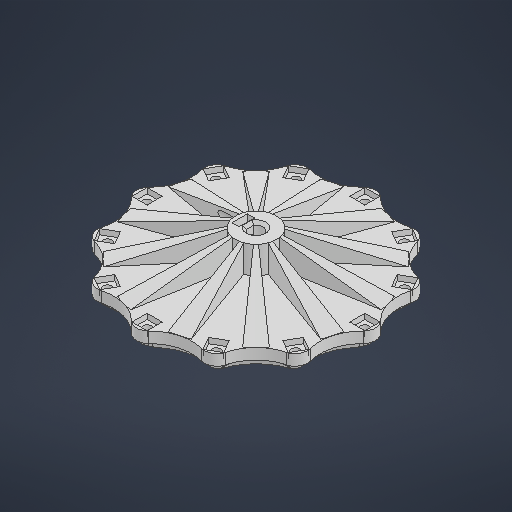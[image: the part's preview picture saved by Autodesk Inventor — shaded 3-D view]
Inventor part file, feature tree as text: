
AUTODESK INVENTOR PART (.ipt)
format: ipt  version: 2025.1 (Build 291241000, 241)  size: 1,274,880 bytes
history: native  units: mm
features: extrude x10, sketch x8, projected_geometry x4, plane x3, pattern_circular x2, chamfer x2, revolve x1
ambient origin geometry x8: Origin, YZ Plane, XZ Plane, XY Plane, X Axis, Y Axis, Z Axis, Center Point
bodies: Solid1 (feature_tree)
feature tree (30):
  sketch  "Sketch1"  dims[d0=5.2mm d3=15.0mm]
  extrude  "Extrusion1"  Depth=15.0mm
  extrude  "Extrusion2"  Depth=3.0mm TaperAngle=0.0deg
  extrude  "Extrusion3"  Depth=10.0mm
  sketch  "Sketch3"  dims[d7=10.0mm d8=0.0mm d9=3.2mm]
  plane  "Work Plane2"
  extrude  "Extrusion4"  TaperAngle=0.0deg  [1 undecoded]
  extrude  "Extrusion5"  Depth=5.65mm
  extrude  "Extrusion7"  Depth=10.0mm
  extrude  "Extrusion11"  TaperAngle=0.0deg  [1 undecoded]
  pattern_circular  "Circular Pattern1"  Count=12 Angle=360.0deg
  sketch  "Sketch4"  dims[d10=5.0mm d11=0.0mm d12=0.0mm]
  plane  "Work Plane3"
  revolve  "Revolution1"  Angle=15.0deg
  pattern_circular  "Circular Pattern2"  [2 undecoded]
  plane  "Work Plane4"
  extrude  "Extrusion8"  Depth=10.0mm
  extrude  "Extrusion9"  Depth=10.0mm
  chamfer  "Chamfer2"  Distance=10.0mm
  extrude  "Extrusion10"  TaperAngle=90.0deg  [1 undecoded]
  chamfer  "Chamfer3"  Distance=1.745329mm
  sketch  "Sketch2"  dims[d4=79.5mm d5=3.0mm d6=0.0mm]
  projected_geometry  "Projected Loop1"
  projected_geometry  "Projected Loop2"
  sketch  "Sketch5"  dims[d13=1.2mm d14=5.65mm]
  projected_geometry  "Projected Loop3"
  sketch  "Sketch7"  dims[d15=2.6mm]
  sketch  "Sketch8"  dims[d16=-5.0mm d17=10.0mm d18=3.0mm d19=0.0mm d20=0.0mm d21=3.2mm]
  projected_geometry  "Projected Loop4"
  sketch  "Sketch9"  dims[d23=40.0mm d24=0.0mm d25=0.0mm d28=120.0mm d29=360.0deg d44=15.0deg d45=15.0deg d46=31.0mm d48=39.75mm d49=4.5mm d50=10.0mm d51=0.0mm d52=90.0deg d53=1.745329mm d54=120.0mm d55=360.0deg d57=6.0mm d58=0.0mm d59=0.0mm d60=5.0mm d61=0.0mm d62=4.0mm d63=2.0mm d64=45.0deg d65=3.4mm d66=3.4mm d67=20.0mm d68=8.0mm d69=0.0mm d70=5.55mm d71=2.0mm d72=0.0mm d73=4.8mm d74=1.0mm d75=2.0mm d76=45.0deg]
note: 5 required parameter values undecoded (feature->parameter linkage not recoverable at this tier; creation-order binding heuristic only, values carry confidence <= 0.55)
